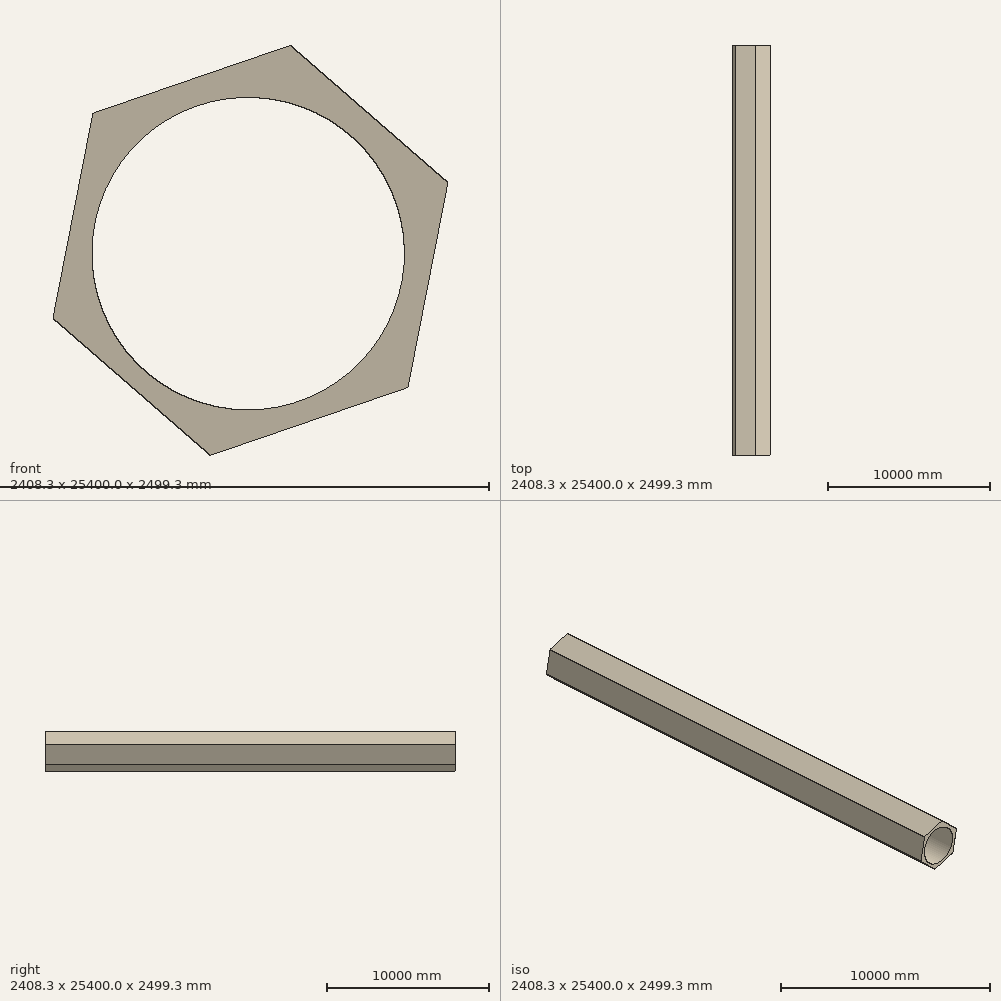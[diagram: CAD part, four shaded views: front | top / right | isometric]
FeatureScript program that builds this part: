
annotation { "Feature Type Name" : "Feature", "Feature Type Description" : "" }
export const myFeature = defineFeature(function(context is Context, id is Id, definition is map)
    precondition{}
    {
        {
            var Q0;
            Q0=qCreatedBy(makeId("Front.planeOp"),FACE);
            var sketch = newSketch(context, id + "F0", { "sketchPlane" : qUnion([Q0])});
            skCircle(sketch, "E0.cCircle", {"center": v(14.04, 26.92) * mm, "radius": 1102.65 * mm, "construction": true});
            skLineSegment(sketch, "E0.0", {"start": v(1218.18, 440.63) * mm, "end": v(974.4, -809.05) * mm});
            skLineSegment(sketch, "E0.1", {"start": v(974.4, -809.05) * mm, "end": v(-229.74, -1222.76) * mm});
            skLineSegment(sketch, "E0.2", {"start": v(-229.74, -1222.76) * mm, "end": v(-1190.1, -386.8) * mm});
            skLineSegment(sketch, "E0.3", {"start": v(-1190.1, -386.8) * mm, "end": v(-946.31, 862.88) * mm});
            skLineSegment(sketch, "E0.4", {"start": v(-946.31, 862.88) * mm, "end": v(257.83, 1276.6) * mm});
            skLineSegment(sketch, "E0.5", {"start": v(257.83, 1276.6) * mm, "end": v(1218.18, 440.63) * mm});
            skPoint(sketch, "E0.0.midPoint", {"position": v(1096.3, -184.2) * mm});
            skSolve(sketch);
        }
        {
            var Q0;
            Q0=makeQuery(id+"F0.imprint","IMPRINT",FACE,{"disambiguationData":[TD([[makeQuery(id+"F0.imprint","IMPRINT",EDGE,{"derivedFrom":sQuery(id+"F0.wireOp",EDGE,"E0.0")}),-1.0]])]});
            extrude(context, id + "F1", {"entities" : qUnion([Q0]), "depth" : 25400 * mm});
        }
        {
            var Q0;
            Q0=makeQuery(id+"F1.opExtrude","CAP_FACE",FACE,{"disambiguationData":[OSD([sQuery(id+"F0.wireOp",EDGE,"E0.0"),sQuery(id+"F0.wireOp",EDGE,"E0.1"),sQuery(id+"F0.wireOp",EDGE,"E0.2"),sQuery(id+"F0.wireOp",EDGE,"E0.3"),sQuery(id+"F0.wireOp",EDGE,"E0.4"),sQuery(id+"F0.wireOp",EDGE,"E0.5")])],"isStart":false});
            var sketch = newSketch(context, id + "F2", { "sketchPlane" : qUnion([Q0])});
            skLineSegment(sketch, "E1", {"start": v(0, 7.52) * mm, "end": v(0, 46.83) * mm});
            skSolve(sketch);
        }
        {
            var Q0;
            Q0=sQuery(id+"F2.wireOp",VERTEX,"E1.start");
            var Q1;
            Q1=makeQuery(id+"F1.opExtrude","SWEPT_BODY",BODY,{"disambiguationData":[OSD([sQuery(id+"F0.wireOp",EDGE,"E0.0"),sQuery(id+"F0.wireOp",EDGE,"E0.1"),sQuery(id+"F0.wireOp",EDGE,"E0.2"),sQuery(id+"F0.wireOp",EDGE,"E0.3"),sQuery(id+"F0.wireOp",EDGE,"E0.4"),sQuery(id+"F0.wireOp",EDGE,"E0.5")])]});
            hole(context, id + "F3", {"style" : HoleStyle.SIMPLE, "endStyle" : HoleEndStyle.THROUGH, "holeDiameter" : 1905 * mm, "tappedDepth" : 12.7 * mm, "tapClearance" : 3, "locations" : qUnion([Q0]), "scope" : qUnion([Q1])});
        }
    });
